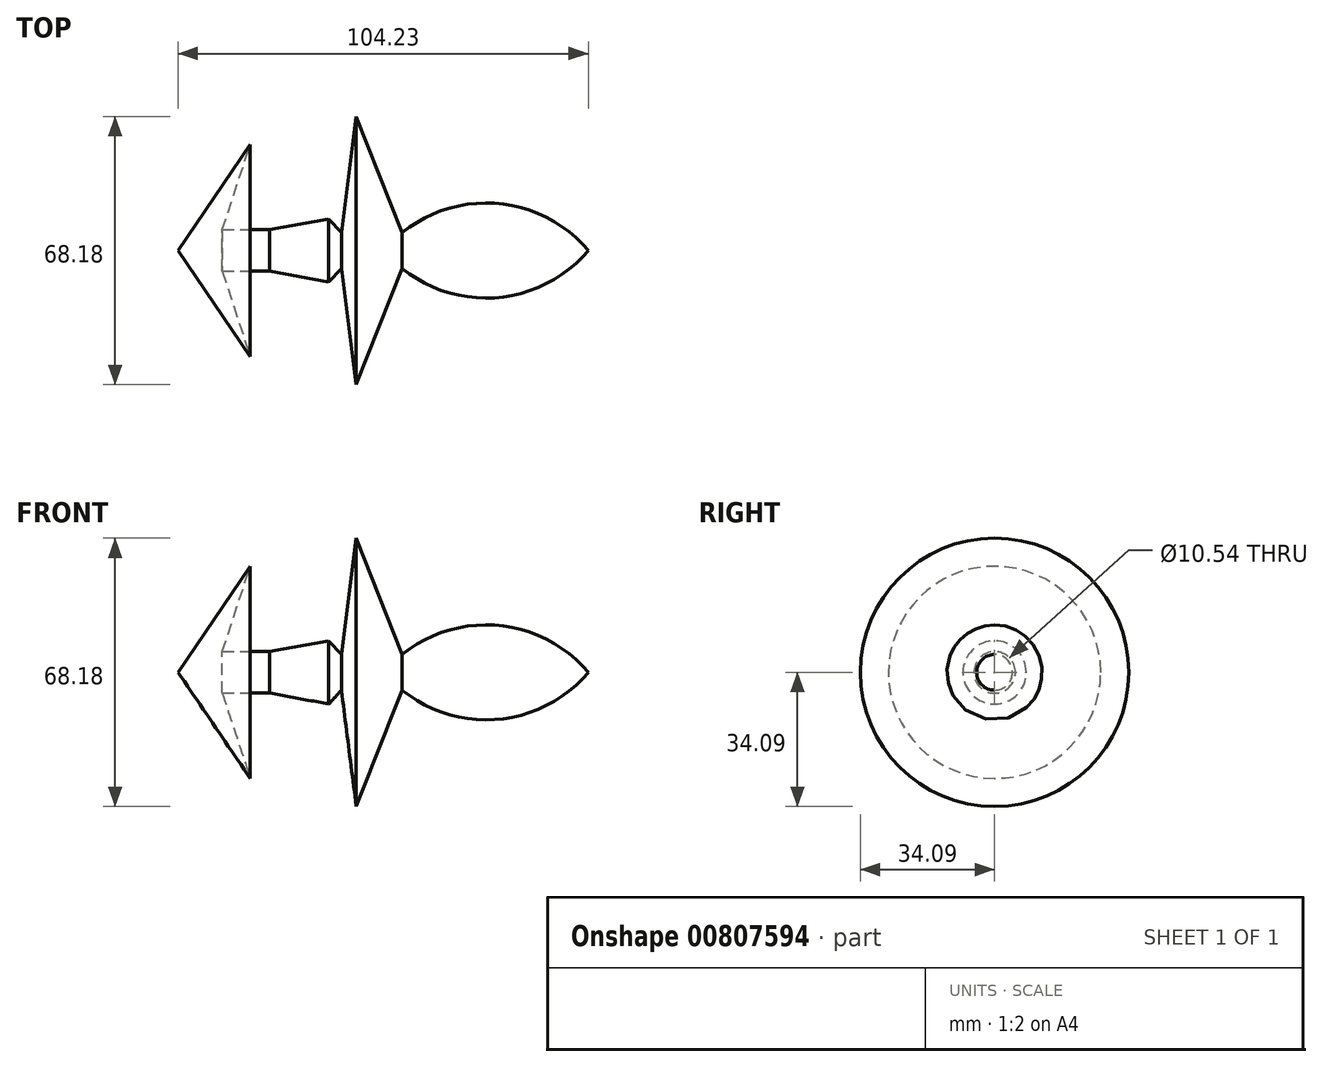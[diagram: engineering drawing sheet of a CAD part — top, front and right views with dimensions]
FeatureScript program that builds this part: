
annotation { "Feature Type Name" : "Feature", "Feature Type Description" : "" }
export const myFeature = defineFeature(function(context is Context, id is Id, definition is map)
    precondition{}
    {
        {
            var Q0;
            Q0=qCreatedBy(makeId("Front.planeOp"),FACE);
            var sketch = newSketch(context, id + "F0", { "sketchPlane" : qUnion([Q0])});
            skLineSegment(sketch, "E0", {"start": v(-49.93, 0) * mm, "end": v(-31.58, 26.96) * mm});
            skLineSegment(sketch, "E1", {"start": v(-31.58, 26.96) * mm, "end": v(-38.72, 5.27) * mm});
            skLineSegment(sketch, "E2", {"start": v(-38.72, 5.27) * mm, "end": v(-26.64, 5.27) * mm});
            skLineSegment(sketch, "E3", {"start": v(-26.64, 5.27) * mm, "end": v(-11.64, 8.04) * mm});
            skLineSegment(sketch, "E4", {"start": v(-11.64, 8.04) * mm, "end": v(-8.44, 4.54) * mm});
            skLineSegment(sketch, "E5", {"start": v(-8.44, 4.54) * mm, "end": v(-4.65, 34.1) * mm});
            skLineSegment(sketch, "E6", {"start": v(-4.65, 34.1) * mm, "end": v(7, 4.54) * mm});
            skArc(sketch, "E7", {"start": v(54.3, 0) * mm, "mid": v(31.57, 11.92) * mm, "end": v(7, 4.54) * mm});
            skLineSegment(sketch, "E8", {"start": v(-66.52, 0) * mm, "end": v(67.98, 0) * mm, "construction": true});
            skSolve(sketch);
        }
        {
            var Q0;
            Q0=sQuery(id+"F0.wireOp",EDGE,"E0");
            var Q1;
            Q1=sQuery(id+"F0.wireOp",EDGE,"E1");
            var Q2;
            Q2=sQuery(id+"F0.wireOp",EDGE,"E3");
            var Q3;
            Q3=sQuery(id+"F0.wireOp",EDGE,"E2");
            var Q4;
            Q4=sQuery(id+"F0.wireOp",EDGE,"E4");
            var Q5;
            Q5=sQuery(id+"F0.wireOp",EDGE,"E5");
            var Q6;
            Q6=sQuery(id+"F0.wireOp",EDGE,"E6");
            var Q7;
            Q7=sQuery(id+"F0.wireOp",EDGE,"E7");
            var Q8;
            Q8=sQuery(id+"F0.wireOp",EDGE,"E8");
            revolve(context, id + "F1", {"bodyType" : ToolBodyType.SURFACE, "surfaceOperationType" : NewSurfaceOperationType.NEW, "surfaceEntities" : qUnion([Q0, Q1, Q2, Q3, Q4, Q5, Q6, Q7]), "axis" : qUnion([Q8]), "revolveType" : RevolveType.FULL});
        }
    });
